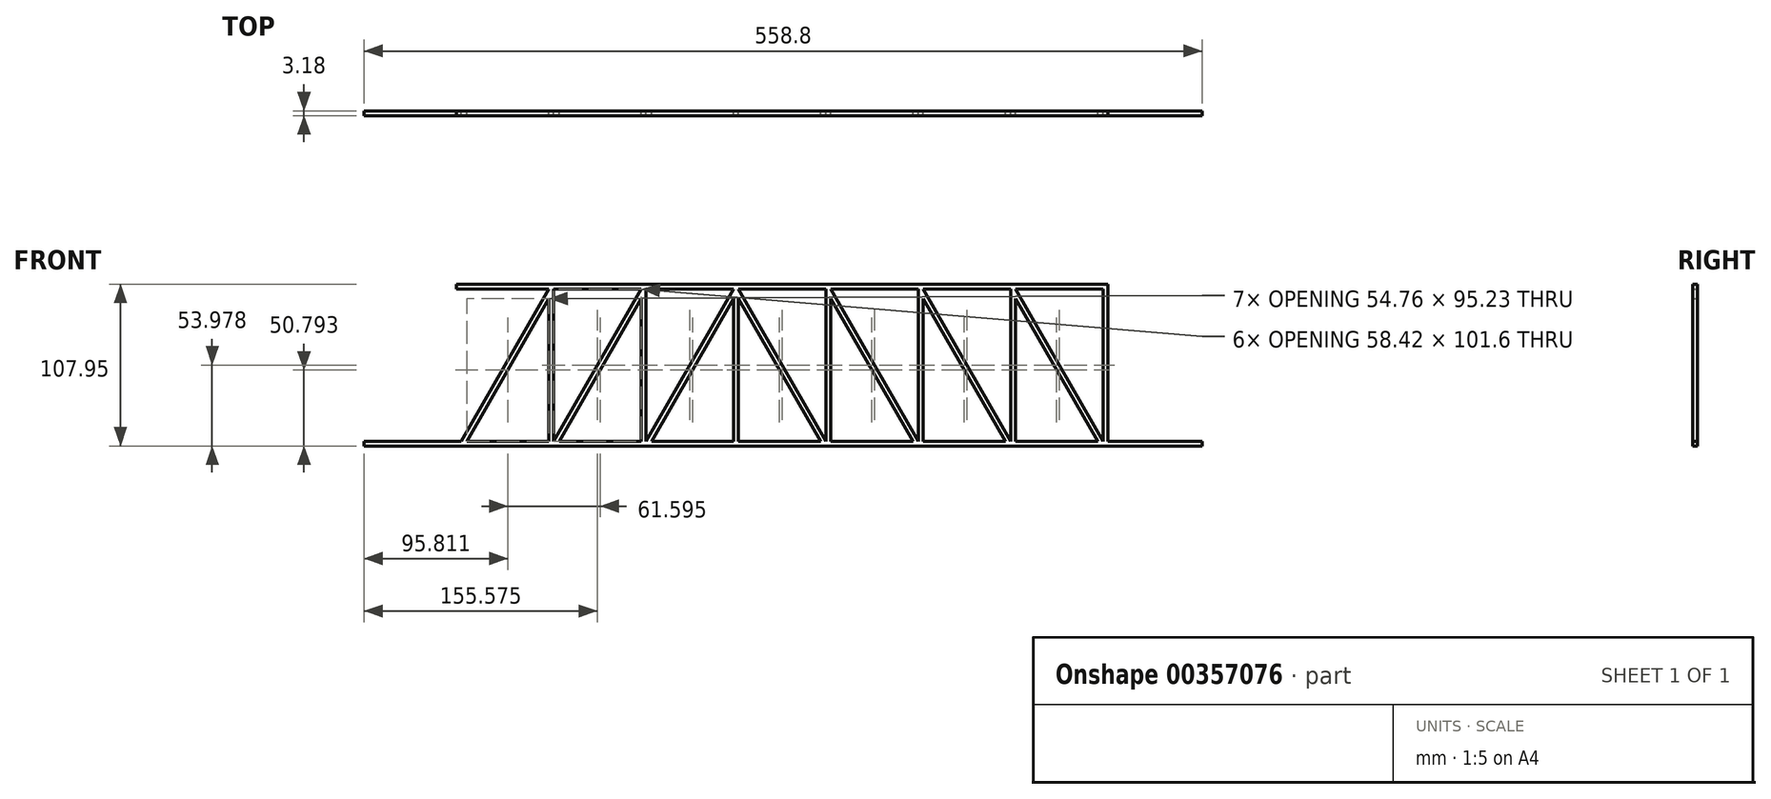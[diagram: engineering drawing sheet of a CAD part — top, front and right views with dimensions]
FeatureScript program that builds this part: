
annotation { "Feature Type Name" : "Feature", "Feature Type Description" : "" }
export const myFeature = defineFeature(function(context is Context, id is Id, definition is map)
    precondition{}
    {
        {
            var Q0;
            Q0=qCreatedBy(makeId("Front.planeOp"),FACE);
            var sketch = newSketch(context, id + "F0", { "sketchPlane" : qUnion([Q0])});
            skLineSegment(sketch, "E0.bottom", {"start": v(279.4, -1.59) * mm, "end": v(-279.4, -1.59) * mm});
            skLineSegment(sketch, "E0.top", {"start": v(279.4, 1.59) * mm, "end": v(-279.4, 1.59) * mm});
            skLineSegment(sketch, "E0.left", {"start": v(279.4, -1.59) * mm, "end": v(279.4, 1.59) * mm});
            skLineSegment(sketch, "E0.right", {"start": v(-279.4, -1.59) * mm, "end": v(-279.4, 1.59) * mm});
            skPoint(sketch, "E0.middle", {"position": v(0, 0) * mm});
            skLineSegment(sketch, "E1", {"start": v(-279.4, 1.59) * mm, "end": v(-276.23, 1.59) * mm});
            skLineSegment(sketch, "E2", {"start": v(-276.23, 1.59) * mm, "end": v(-217.8, 1.59) * mm});
            skLineSegment(sketch, "E3", {"start": v(-217.8, 1.59) * mm, "end": v(-214.63, 1.59) * mm});
            skLineSegment(sketch, "E4", {"start": v(-217.8, 1.59) * mm, "end": v(-217.8, 103.19) * mm});
            skLineSegment(sketch, "E5", {"start": v(-214.63, 1.59) * mm, "end": v(-214.63, 103.19) * mm});
            skLineSegment(sketch, "E6", {"start": v(-217.8, 103.19) * mm, "end": v(-214.63, 103.19) * mm});
            skLineSegment(sketch, "E7", {"start": v(-217.8, 103.19) * mm, "end": v(-279.4, 1.59) * mm});
            skLineSegment(sketch, "E8", {"start": v(-276.23, 1.59) * mm, "end": v(-217.8, 97.95) * mm});
            skLineSegment(sketch, "E9", {"start": v(-217.8, 97.95) * mm, "end": v(-217.8, 103.19) * mm});
            skLineSegment(sketch, "E10.1.0.0", {"start": v(-156.21, 1.59) * mm, "end": v(-156.21, 103.19) * mm});
            skLineSegment(sketch, "E10.1.0.1", {"start": v(-153.04, 1.59) * mm, "end": v(-153.04, 103.19) * mm});
            skLineSegment(sketch, "E10.1.0.2", {"start": v(-156.21, 1.59) * mm, "end": v(-153.04, 1.59) * mm});
            skLineSegment(sketch, "E10.1.0.3", {"start": v(-156.21, 103.19) * mm, "end": v(-153.04, 103.19) * mm});
            skLineSegment(sketch, "E10.2.0.0", {"start": v(-94.62, 1.59) * mm, "end": v(-94.62, 103.19) * mm});
            skLineSegment(sketch, "E10.2.0.1", {"start": v(-91.44, 1.59) * mm, "end": v(-91.44, 103.19) * mm});
            skLineSegment(sketch, "E10.2.0.2", {"start": v(-94.62, 1.59) * mm, "end": v(-91.44, 1.59) * mm});
            skLineSegment(sketch, "E10.2.0.3", {"start": v(-94.62, 103.19) * mm, "end": v(-91.44, 103.19) * mm});
            skLineSegment(sketch, "E10.direction1", {"start": v(-217.8, 1.59) * mm, "end": v(-156.21, 1.59) * mm, "construction": true});
            skLineSegment(sketch, "E11.0.3.0", {"start": v(-33.02, 1.59) * mm, "end": v(-33.02, 103.19) * mm});
            skLineSegment(sketch, "E11.3.3.0", {"start": v(-29.85, 1.59) * mm, "end": v(-29.85, 103.19) * mm});
            skLineSegment(sketch, "E11.6.3.0", {"start": v(-33.02, 1.59) * mm, "end": v(-29.85, 1.59) * mm});
            skLineSegment(sketch, "E11.9.3.0", {"start": v(-33.02, 103.19) * mm, "end": v(-29.85, 103.19) * mm});
            skLineSegment(sketch, "E11.0.4.0", {"start": v(28.57, 1.59) * mm, "end": v(28.57, 103.19) * mm});
            skLineSegment(sketch, "E11.3.4.0", {"start": v(31.75, 1.59) * mm, "end": v(31.75, 103.19) * mm});
            skLineSegment(sketch, "E11.6.4.0", {"start": v(28.57, 1.59) * mm, "end": v(31.75, 1.59) * mm});
            skLineSegment(sketch, "E11.9.4.0", {"start": v(28.57, 103.19) * mm, "end": v(31.75, 103.19) * mm});
            skLineSegment(sketch, "E11.0.5.0", {"start": v(90.17, 1.59) * mm, "end": v(90.17, 103.19) * mm});
            skLineSegment(sketch, "E11.3.5.0", {"start": v(93.35, 1.59) * mm, "end": v(93.34, 103.19) * mm});
            skLineSegment(sketch, "E11.6.5.0", {"start": v(90.17, 1.59) * mm, "end": v(93.35, 1.59) * mm});
            skLineSegment(sketch, "E11.9.5.0", {"start": v(90.17, 103.19) * mm, "end": v(93.34, 103.19) * mm});
            skLineSegment(sketch, "E11.0.6.0", {"start": v(151.77, 1.59) * mm, "end": v(151.76, 103.19) * mm});
            skLineSegment(sketch, "E11.3.6.0", {"start": v(154.94, 1.59) * mm, "end": v(154.94, 103.19) * mm});
            skLineSegment(sketch, "E11.6.6.0", {"start": v(151.77, 1.59) * mm, "end": v(154.94, 1.59) * mm});
            skLineSegment(sketch, "E11.9.6.0", {"start": v(151.76, 103.19) * mm, "end": v(154.94, 103.19) * mm});
            skLineSegment(sketch, "E11.0.7.0", {"start": v(213.36, 1.59) * mm, "end": v(213.36, 103.19) * mm});
            skLineSegment(sketch, "E11.3.7.0", {"start": v(216.54, 1.59) * mm, "end": v(216.53, 103.19) * mm});
            skLineSegment(sketch, "E11.6.7.0", {"start": v(213.36, 1.59) * mm, "end": v(216.54, 1.59) * mm});
            skLineSegment(sketch, "E11.9.7.0", {"start": v(213.36, 103.19) * mm, "end": v(216.53, 103.19) * mm});
            skLineSegment(sketch, "E12", {"start": v(279.4, 1.59) * mm, "end": v(276.23, 1.59) * mm});
            skLineSegment(sketch, "E13", {"start": v(216.53, 103.19) * mm, "end": v(279.4, 1.59) * mm});
            skLineSegment(sketch, "E14", {"start": v(276.23, 1.59) * mm, "end": v(216.53, 98.06) * mm});
            skLineSegment(sketch, "E15", {"start": v(216.54, 98.06) * mm, "end": v(216.54, 103.19) * mm});
            skLineSegment(sketch, "E16.bottom", {"start": v(-217.8, 103.19) * mm, "end": v(216.53, 103.19) * mm});
            skLineSegment(sketch, "E16.top", {"start": v(-217.8, 106.36) * mm, "end": v(216.54, 106.36) * mm});
            skLineSegment(sketch, "E16.left", {"start": v(-217.8, 103.19) * mm, "end": v(-217.8, 106.36) * mm});
            skLineSegment(sketch, "E16.right", {"start": v(216.53, 103.19) * mm, "end": v(216.53, 106.36) * mm});
            skLineSegment(sketch, "E17", {"start": v(-156.21, 103.19) * mm, "end": v(-214.63, 1.59) * mm});
            skLineSegment(sketch, "E18", {"start": v(-214.63, 1.59) * mm, "end": v(-210.97, 1.59) * mm});
            skLineSegment(sketch, "E19", {"start": v(-210.97, 1.59) * mm, "end": v(-156.21, 96.82) * mm});
            skLineSegment(sketch, "E20", {"start": v(-156.21, 96.82) * mm, "end": v(-156.21, 103.19) * mm});
            skLineSegment(sketch, "E21.1.0.0", {"start": v(-149.37, 1.59) * mm, "end": v(-94.62, 96.82) * mm});
            skLineSegment(sketch, "E21.1.0.1", {"start": v(-94.62, 103.19) * mm, "end": v(-153.04, 1.59) * mm});
            skLineSegment(sketch, "E21.1.0.2", {"start": v(-94.62, 96.82) * mm, "end": v(-94.62, 103.19) * mm});
            skLineSegment(sketch, "E21.1.0.3", {"start": v(-153.03, 1.59) * mm, "end": v(-149.37, 1.59) * mm});
            skLineSegment(sketch, "E21.2.0.0", {"start": v(-87.78, 1.59) * mm, "end": v(-33.02, 96.82) * mm});
            skLineSegment(sketch, "E21.2.0.1", {"start": v(-33.02, 103.19) * mm, "end": v(-91.44, 1.59) * mm});
            skLineSegment(sketch, "E21.2.0.2", {"start": v(-33.02, 96.82) * mm, "end": v(-33.02, 103.19) * mm});
            skLineSegment(sketch, "E21.2.0.3", {"start": v(-91.44, 1.59) * mm, "end": v(-87.78, 1.59) * mm});
            skLineSegment(sketch, "E21.direction1", {"start": v(-214.63, 1.59) * mm, "end": v(-153.03, 1.59) * mm, "construction": true});
            skLineSegment(sketch, "E22", {"start": v(154.94, 103.19) * mm, "end": v(213.36, 1.59) * mm});
            skLineSegment(sketch, "E23", {"start": v(154.94, 103.19) * mm, "end": v(154.94, 96.82) * mm});
            skLineSegment(sketch, "E24", {"start": v(154.94, 96.82) * mm, "end": v(209.7, 1.59) * mm});
            skLineSegment(sketch, "E25", {"start": v(209.7, 1.59) * mm, "end": v(213.36, 1.59) * mm});
            skLineSegment(sketch, "E26.1.0.0", {"start": v(93.34, 103.19) * mm, "end": v(151.76, 1.59) * mm});
            skLineSegment(sketch, "E26.1.0.1", {"start": v(93.34, 96.82) * mm, "end": v(148.1, 1.59) * mm});
            skLineSegment(sketch, "E26.1.0.2", {"start": v(93.34, 103.19) * mm, "end": v(93.34, 96.82) * mm});
            skLineSegment(sketch, "E26.1.0.3", {"start": v(90.17, 1.59) * mm, "end": v(93.34, 1.59) * mm});
            skLineSegment(sketch, "E26.1.0.4", {"start": v(148.1, 1.59) * mm, "end": v(151.76, 1.59) * mm});
            skLineSegment(sketch, "E26.2.0.0", {"start": v(31.75, 103.19) * mm, "end": v(90.17, 1.59) * mm});
            skLineSegment(sketch, "E26.2.0.1", {"start": v(31.75, 96.82) * mm, "end": v(86.5, 1.59) * mm});
            skLineSegment(sketch, "E26.2.0.2", {"start": v(31.75, 103.19) * mm, "end": v(31.75, 96.82) * mm});
            skLineSegment(sketch, "E26.2.0.4", {"start": v(86.5, 1.59) * mm, "end": v(90.17, 1.59) * mm});
            skLineSegment(sketch, "E26.direction1", {"start": v(151.77, 1.59) * mm, "end": v(90.17, 1.59) * mm, "construction": true});
            skLineSegment(sketch, "E27.0.3.0", {"start": v(-29.85, 103.19) * mm, "end": v(28.57, 1.59) * mm});
            skLineSegment(sketch, "E27.3.3.0", {"start": v(-29.85, 96.82) * mm, "end": v(24.91, 1.59) * mm});
            skLineSegment(sketch, "E27.6.3.0", {"start": v(-29.85, 103.19) * mm, "end": v(-29.85, 96.82) * mm});
            skLineSegment(sketch, "E27.12.3.0", {"start": v(24.91, 1.59) * mm, "end": v(28.57, 1.59) * mm});
            skSolve(sketch);
        }
        {
            var Q0;
            Q0=makeQuery(id+"F0.imprint","IMPRINT",FACE,{"disambiguationData":[TD([[makeQuery(id+"F0.imprint","IMPRINT",EDGE,{"derivedFrom":sQuery(id+"F0.wireOp",EDGE,"E1")}),1.0]])]});
            var Q1;
            Q1=makeQuery(id+"F0.imprint","IMPRINT",FACE,{"disambiguationData":[TD([[makeQuery(id+"F0.imprint","IMPRINT",EDGE,{"derivedFrom":sQuery(id+"F0.wireOp",EDGE,"E0.bottom")}),-1.0]])]});
            var Q2;
            Q2=makeQuery(id+"F0.imprint","IMPRINT",FACE,{"disambiguationData":[TD([[makeQuery(id+"F0.imprint","IMPRINT",EDGE,{"derivedFrom":sQuery(id+"F0.wireOp",EDGE,"E16.top")}),-1.0]])]});
            var Q3;
            Q3=makeQuery(id+"F0.imprint","IMPRINT",FACE,{"disambiguationData":[TD([[makeQuery(id+"F0.imprint","IMPRINT",EDGE,{"derivedFrom":sQuery(id+"F0.wireOp",EDGE,"E3")}),1.0]])]});
            var Q4;
            Q4=makeQuery(id+"F0.imprint","IMPRINT",FACE,{"disambiguationData":[TD([[makeQuery(id+"F0.imprint","IMPRINT",EDGE,{"derivedFrom":sQuery(id+"F0.wireOp",EDGE,"E17")}),1.0]])]});
            var Q5;
            Q5=makeQuery(id+"F0.imprint","IMPRINT",FACE,{"disambiguationData":[TD([[makeQuery(id+"F0.imprint","IMPRINT",EDGE,{"derivedFrom":sQuery(id+"F0.wireOp",EDGE,"E10.1.0.0")}),-1.0]])]});
            var Q6;
            Q6=makeQuery(id+"F0.imprint","IMPRINT",FACE,{"disambiguationData":[TD([[makeQuery(id+"F0.imprint","IMPRINT",EDGE,{"derivedFrom":sQuery(id+"F0.wireOp",EDGE,"E21.1.0.0")}),1.0]])]});
            var Q7;
            Q7=makeQuery(id+"F0.imprint","IMPRINT",FACE,{"disambiguationData":[TD([[makeQuery(id+"F0.imprint","IMPRINT",EDGE,{"derivedFrom":sQuery(id+"F0.wireOp",EDGE,"E10.2.0.0")}),-1.0]])]});
            var Q8;
            Q8=makeQuery(id+"F0.imprint","IMPRINT",FACE,{"disambiguationData":[TD([[makeQuery(id+"F0.imprint","IMPRINT",EDGE,{"derivedFrom":sQuery(id+"F0.wireOp",EDGE,"E21.2.0.0")}),1.0]])]});
            var Q9;
            Q9=makeQuery(id+"F0.imprint","IMPRINT",FACE,{"disambiguationData":[TD([[makeQuery(id+"F0.imprint","IMPRINT",EDGE,{"derivedFrom":sQuery(id+"F0.wireOp",EDGE,"E11.0.3.0")}),-1.0]])]});
            var Q10;
            {var subQ1=sQuery(id+"F0.wireOp",EDGE,"E11.0.4.0");Q10=makeQuery(id+"F0.imprint","IMPRINT",FACE,{"disambiguationData":[TD([[makeQuery(id+"F0.imprint","IMPRINT",EDGE,{"derivedFrom":subQ1}),-1.0]])]});}
            var Q11;
            Q11=makeQuery(id+"F0.imprint","IMPRINT",FACE,{"disambiguationData":[TD([[makeQuery(id+"F0.imprint","IMPRINT",EDGE,{"derivedFrom":sQuery(id+"F0.wireOp",EDGE,"E27.0.3.0")}),-1.0]])]});
            var Q12;
            Q12=makeQuery(id+"F0.imprint","IMPRINT",FACE,{"disambiguationData":[TD([[makeQuery(id+"F0.imprint","IMPRINT",EDGE,{"derivedFrom":sQuery(id+"F0.wireOp",EDGE,"E26.2.0.0")}),-1.0]])]});
            var Q13;
            {var subQ2=sQuery(id+"F0.wireOp",EDGE,"E11.0.5.0");Q13=makeQuery(id+"F0.imprint","IMPRINT",FACE,{"disambiguationData":[TD([[makeQuery(id+"F0.imprint","IMPRINT",EDGE,{"derivedFrom":subQ2}),-1.0]])]});}
            var Q14;
            Q14=makeQuery(id+"F0.imprint","IMPRINT",FACE,{"disambiguationData":[TD([[makeQuery(id+"F0.imprint","IMPRINT",EDGE,{"derivedFrom":sQuery(id+"F0.wireOp",EDGE,"E26.1.0.0")}),-1.0]])]});
            var Q15;
            {var subQ1=sQuery(id+"F0.wireOp",EDGE,"E11.0.6.0");Q15=makeQuery(id+"F0.imprint","IMPRINT",FACE,{"disambiguationData":[TD([[makeQuery(id+"F0.imprint","IMPRINT",EDGE,{"derivedFrom":subQ1}),-1.0]])]});}
            var Q16;
            Q16=makeQuery(id+"F0.imprint","IMPRINT",FACE,{"disambiguationData":[TD([[makeQuery(id+"F0.imprint","IMPRINT",EDGE,{"derivedFrom":sQuery(id+"F0.wireOp",EDGE,"E22")}),-1.0]])]});
            var Q17;
            Q17=makeQuery(id+"F0.imprint","IMPRINT",FACE,{"disambiguationData":[TD([[makeQuery(id+"F0.imprint","IMPRINT",EDGE,{"derivedFrom":sQuery(id+"F0.wireOp",EDGE,"E12")}),-1.0]])]});
            var Q18;
            {var subQ1=sQuery(id+"F0.wireOp",EDGE,"E11.0.7.0");Q18=makeQuery(id+"F0.imprint","IMPRINT",FACE,{"disambiguationData":[TD([[makeQuery(id+"F0.imprint","IMPRINT",EDGE,{"derivedFrom":subQ1}),-1.0]])]});}
            extrude(context, id + "F1", {"entities" : qUnion([Q0, Q1, Q2, Q3, Q4, Q5, Q6, Q7, Q8, Q9, Q10, Q11, Q12, Q13, Q14, Q15, Q16, Q17, Q18]), "endBound" : BoundingType.SYMMETRIC, "depth" : 3.17 * mm});
        }
    });
